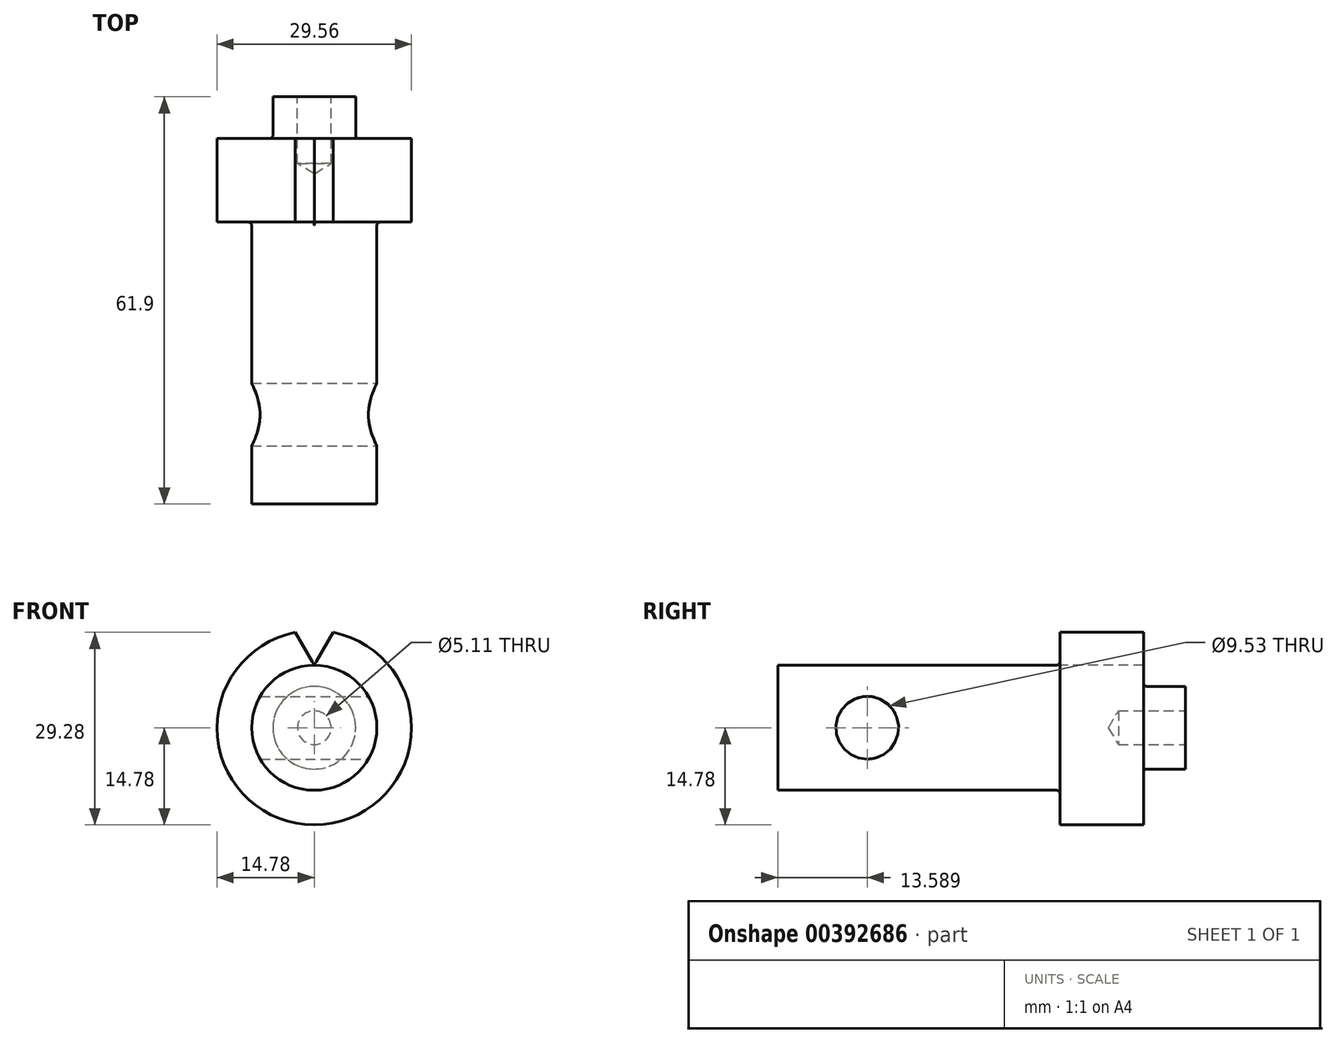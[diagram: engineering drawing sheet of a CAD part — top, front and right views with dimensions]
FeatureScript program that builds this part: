
annotation { "Feature Type Name" : "Feature", "Feature Type Description" : "" }
export const myFeature = defineFeature(function(context is Context, id is Id, definition is map)
    precondition{}
    {
        {
            var Q0;
            Q0=qCreatedBy(makeId("Right.planeOp"),FACE);
            var sketch = newSketch(context, id + "F0", { "sketchPlane" : qUnion([Q0])});
            skLineSegment(sketch, "E0", {"start": v(-42.85, 0) * mm, "end": v(-42.85, 9.51) * mm});
            skLineSegment(sketch, "E1", {"start": v(-42.85, 9.51) * mm, "end": v(0, 9.51) * mm});
            skLineSegment(sketch, "E2", {"start": v(0, 9.51) * mm, "end": v(0, 14.78) * mm});
            skLineSegment(sketch, "E3", {"start": v(0, 14.78) * mm, "end": v(12.7, 14.78) * mm});
            skLineSegment(sketch, "E4", {"start": v(12.7, 14.78) * mm, "end": v(12.7, 6.29) * mm});
            skLineSegment(sketch, "E5", {"start": v(12.7, 6.29) * mm, "end": v(19.05, 6.29) * mm});
            skLineSegment(sketch, "E6", {"start": v(19.05, 6.29) * mm, "end": v(19.05, 0) * mm});
            skLineSegment(sketch, "E7", {"start": v(19.05, 0) * mm, "end": v(-42.85, 0) * mm});
            skSolve(sketch);
        }
        {
            var Q0;
            Q0=makeQuery(id+"F0.imprint","IMPRINT",FACE,{"disambiguationData":[TD([[makeQuery(id+"F0.imprint","IMPRINT",EDGE,{"derivedFrom":sQuery(id+"F0.wireOp",EDGE,"E0")}),-1.0]])]});
            var Q1;
            Q1=sQuery(id+"F0.wireOp",EDGE,"E7");
            revolve(context, id + "F1", {"entities" : qUnion([Q0]), "axis" : qUnion([Q1]), "revolveType" : RevolveType.FULL});
        }
        {
            var Q0;
            Q0=qCreatedBy(makeId("Front.planeOp"),FACE);
            var sketch = newSketch(context, id + "F2", { "sketchPlane" : qUnion([Q0])});
            skLineSegment(sketch, "E8", {"start": v(-2.88, 14.5) * mm, "end": v(0, 9.51) * mm});
            skLineSegment(sketch, "E9", {"start": v(0, 9.51) * mm, "end": v(2.88, 14.5) * mm});
            skArc(sketch, "E10", {"start": v(2.88, 14.5) * mm, "mid": v(0, 14.78) * mm, "end": v(-2.88, 14.5) * mm});
            skSolve(sketch);
        }
        {
            var Q0;
            Q0=makeQuery(id+"F2.imprint","IMPRINT",FACE,{"disambiguationData":[TD([[makeQuery(id+"F2.imprint","IMPRINT",EDGE,{"derivedFrom":sQuery(id+"F2.wireOp",EDGE,"E8")}),1.0]])]});
            extrude(context, id + "F3", {"entities" : qUnion([Q0]), "operationType" : NewBodyOperationType.REMOVE, "oppositeDirection" : true, "depth" : 25.4 * mm});
        }
        {
            var Q0;
            {var subQ2=sQuery(id+"F2.wireOp",EDGE,"E8");var subQ3=makeQuery(id+"F3.boolean.opBoolean","COPY",FACE,{"derivedFrom":makeQuery(id+"F3.opExtrude","SWEPT_FACE",FACE,{"disambiguationData":[OSD([subQ2])]})});var subQ4=sQuery(id+"F0.wireOp",EDGE,"E2");var subQ6=sQuery(id+"F0.wireOp",EDGE,"E1");Q0=makeQuery(id+"Fc7hDyY51l4ybGJ_1.11.F3.boolean.opBoolean","SPLIT",EDGE,{"disambiguationData":[TD([subQ3])],"derivedFrom":makeQuery(id+"Fc7hDyY51l4ybGJ_1.10.F3.boolean.opBoolean","SPLIT",EDGE,{"disambiguationData":[TD([subQ3])],"derivedFrom":makeQuery(id+"Fc7hDyY51l4ybGJ_1.9.F3.boolean.opBoolean","SPLIT",EDGE,{"disambiguationData":[TD([subQ3])],"derivedFrom":makeQuery(id+"Fc7hDyY51l4ybGJ_1.8.F3.boolean.opBoolean","SPLIT",EDGE,{"disambiguationData":[TD([subQ3])],"derivedFrom":makeQuery(id+"Fc7hDyY51l4ybGJ_1.7.F3.boolean.opBoolean","SPLIT",EDGE,{"disambiguationData":[TD([subQ3])],"derivedFrom":makeQuery(id+"Fc7hDyY51l4ybGJ_1.6.F3.boolean.opBoolean","SPLIT",EDGE,{"disambiguationData":[TD([subQ3])],"derivedFrom":makeQuery(id+"Fc7hDyY51l4ybGJ_1.5.F3.boolean.opBoolean","SPLIT",EDGE,{"disambiguationData":[TD([subQ3])],"derivedFrom":makeQuery(id+"Fc7hDyY51l4ybGJ_1.4.F3.boolean.opBoolean","SPLIT",EDGE,{"disambiguationData":[TD([subQ3])],"derivedFrom":makeQuery(id+"Fc7hDyY51l4ybGJ_1.3.F3.boolean.opBoolean","SPLIT",EDGE,{"disambiguationData":[TD([subQ3])],"derivedFrom":makeQuery(id+"Fc7hDyY51l4ybGJ_1.2.F3.boolean.opBoolean","SPLIT",EDGE,{"disambiguationData":[TD([subQ3])],"derivedFrom":makeQuery(id+"Fc7hDyY51l4ybGJ_1.1.F3.boolean.opBoolean","SPLIT",EDGE,{"disambiguationData":[OD(0.0)],"derivedFrom":makeQuery(id+"F1.opRevolve","SWEPT_EDGE",EDGE,{"disambiguationData":[OSD([subQ6,subQ4])]})})})})})})})})})})})});}
            var Q1;
            {var subQ2=sQuery(id+"F2.wireOp",EDGE,"E8");var subQ3=makeQuery(id+"Fc7hDyY51l4ybGJ_1.10.F3.opExtrude","SWEPT_FACE",FACE,{"disambiguationData":[OSD([subQ2])]});var subQ4=sQuery(id+"F0.wireOp",EDGE,"E2");var subQ6=sQuery(id+"F0.wireOp",EDGE,"E1");var subQ9=makeQuery(id+"F3.boolean.opBoolean","COPY",FACE,{"derivedFrom":makeQuery(id+"F3.opExtrude","SWEPT_FACE",FACE,{"disambiguationData":[OSD([subQ2])]})});Q1=makeQuery(id+"Fc7hDyY51l4ybGJ_1.11.F3.boolean.opBoolean","SPLIT",EDGE,{"disambiguationData":[TD([makeQuery(id+"Fc7hDyY51l4ybGJ_1.10.F3.boolean.opBoolean","COPY",FACE,{"derivedFrom":subQ3})])],"derivedFrom":makeQuery(id+"Fc7hDyY51l4ybGJ_1.10.F3.boolean.opBoolean","SPLIT",EDGE,{"disambiguationData":[TD([subQ9])],"derivedFrom":makeQuery(id+"Fc7hDyY51l4ybGJ_1.9.F3.boolean.opBoolean","SPLIT",EDGE,{"disambiguationData":[TD([subQ9])],"derivedFrom":makeQuery(id+"Fc7hDyY51l4ybGJ_1.8.F3.boolean.opBoolean","SPLIT",EDGE,{"disambiguationData":[TD([subQ9])],"derivedFrom":makeQuery(id+"Fc7hDyY51l4ybGJ_1.7.F3.boolean.opBoolean","SPLIT",EDGE,{"disambiguationData":[TD([subQ9])],"derivedFrom":makeQuery(id+"Fc7hDyY51l4ybGJ_1.6.F3.boolean.opBoolean","SPLIT",EDGE,{"disambiguationData":[TD([subQ9])],"derivedFrom":makeQuery(id+"Fc7hDyY51l4ybGJ_1.5.F3.boolean.opBoolean","SPLIT",EDGE,{"disambiguationData":[TD([subQ9])],"derivedFrom":makeQuery(id+"Fc7hDyY51l4ybGJ_1.4.F3.boolean.opBoolean","SPLIT",EDGE,{"disambiguationData":[TD([subQ9])],"derivedFrom":makeQuery(id+"Fc7hDyY51l4ybGJ_1.3.F3.boolean.opBoolean","SPLIT",EDGE,{"disambiguationData":[TD([subQ9])],"derivedFrom":makeQuery(id+"Fc7hDyY51l4ybGJ_1.2.F3.boolean.opBoolean","SPLIT",EDGE,{"disambiguationData":[TD([subQ9])],"derivedFrom":makeQuery(id+"Fc7hDyY51l4ybGJ_1.1.F3.boolean.opBoolean","SPLIT",EDGE,{"disambiguationData":[OD(0.0)],"derivedFrom":makeQuery(id+"F1.opRevolve","SWEPT_EDGE",EDGE,{"disambiguationData":[OSD([subQ6,subQ4])]})})})})})})})})})})})});}
            var Q2;
            {var subQ2=sQuery(id+"F0.wireOp",EDGE,"E1");var subQ4=sQuery(id+"F2.wireOp",EDGE,"E8");var subQ5=makeQuery(id+"Fc7hDyY51l4ybGJ_1.9.F3.opExtrude","SWEPT_FACE",FACE,{"disambiguationData":[OSD([subQ4])]});var subQ6=sQuery(id+"F0.wireOp",EDGE,"E2");var subQ9=makeQuery(id+"F3.boolean.opBoolean","COPY",FACE,{"derivedFrom":makeQuery(id+"F3.opExtrude","SWEPT_FACE",FACE,{"disambiguationData":[OSD([subQ4])]})});Q2=makeQuery(id+"Fc7hDyY51l4ybGJ_1.10.F3.boolean.opBoolean","SPLIT",EDGE,{"disambiguationData":[TD([makeQuery(id+"Fc7hDyY51l4ybGJ_1.9.F3.boolean.opBoolean","COPY",FACE,{"derivedFrom":subQ5})])],"derivedFrom":makeQuery(id+"Fc7hDyY51l4ybGJ_1.9.F3.boolean.opBoolean","SPLIT",EDGE,{"disambiguationData":[TD([subQ9])],"derivedFrom":makeQuery(id+"Fc7hDyY51l4ybGJ_1.8.F3.boolean.opBoolean","SPLIT",EDGE,{"disambiguationData":[TD([subQ9])],"derivedFrom":makeQuery(id+"Fc7hDyY51l4ybGJ_1.7.F3.boolean.opBoolean","SPLIT",EDGE,{"disambiguationData":[TD([subQ9])],"derivedFrom":makeQuery(id+"Fc7hDyY51l4ybGJ_1.6.F3.boolean.opBoolean","SPLIT",EDGE,{"disambiguationData":[TD([subQ9])],"derivedFrom":makeQuery(id+"Fc7hDyY51l4ybGJ_1.5.F3.boolean.opBoolean","SPLIT",EDGE,{"disambiguationData":[TD([subQ9])],"derivedFrom":makeQuery(id+"Fc7hDyY51l4ybGJ_1.4.F3.boolean.opBoolean","SPLIT",EDGE,{"disambiguationData":[TD([subQ9])],"derivedFrom":makeQuery(id+"Fc7hDyY51l4ybGJ_1.3.F3.boolean.opBoolean","SPLIT",EDGE,{"disambiguationData":[TD([subQ9])],"derivedFrom":makeQuery(id+"Fc7hDyY51l4ybGJ_1.2.F3.boolean.opBoolean","SPLIT",EDGE,{"disambiguationData":[TD([subQ9])],"derivedFrom":makeQuery(id+"Fc7hDyY51l4ybGJ_1.1.F3.boolean.opBoolean","SPLIT",EDGE,{"disambiguationData":[OD(0.0)],"derivedFrom":makeQuery(id+"F1.opRevolve","SWEPT_EDGE",EDGE,{"disambiguationData":[OSD([subQ2,subQ6])]})})})})})})})})})})});}
            var Q3;
            {var subQ0=sQuery(id+"F2.wireOp",EDGE,"E8");var subQ1=makeQuery(id+"Fc7hDyY51l4ybGJ_1.8.F3.opExtrude","SWEPT_FACE",FACE,{"disambiguationData":[OSD([subQ0])]});var subQ2=sQuery(id+"F0.wireOp",EDGE,"E2");var subQ6=sQuery(id+"F0.wireOp",EDGE,"E1");var subQ9=makeQuery(id+"F3.boolean.opBoolean","COPY",FACE,{"derivedFrom":makeQuery(id+"F3.opExtrude","SWEPT_FACE",FACE,{"disambiguationData":[OSD([subQ0])]})});Q3=makeQuery(id+"Fc7hDyY51l4ybGJ_1.9.F3.boolean.opBoolean","SPLIT",EDGE,{"disambiguationData":[TD([makeQuery(id+"Fc7hDyY51l4ybGJ_1.8.F3.boolean.opBoolean","COPY",FACE,{"derivedFrom":subQ1})])],"derivedFrom":makeQuery(id+"Fc7hDyY51l4ybGJ_1.8.F3.boolean.opBoolean","SPLIT",EDGE,{"disambiguationData":[TD([subQ9])],"derivedFrom":makeQuery(id+"Fc7hDyY51l4ybGJ_1.7.F3.boolean.opBoolean","SPLIT",EDGE,{"disambiguationData":[TD([subQ9])],"derivedFrom":makeQuery(id+"Fc7hDyY51l4ybGJ_1.6.F3.boolean.opBoolean","SPLIT",EDGE,{"disambiguationData":[TD([subQ9])],"derivedFrom":makeQuery(id+"Fc7hDyY51l4ybGJ_1.5.F3.boolean.opBoolean","SPLIT",EDGE,{"disambiguationData":[TD([subQ9])],"derivedFrom":makeQuery(id+"Fc7hDyY51l4ybGJ_1.4.F3.boolean.opBoolean","SPLIT",EDGE,{"disambiguationData":[TD([subQ9])],"derivedFrom":makeQuery(id+"Fc7hDyY51l4ybGJ_1.3.F3.boolean.opBoolean","SPLIT",EDGE,{"disambiguationData":[TD([subQ9])],"derivedFrom":makeQuery(id+"Fc7hDyY51l4ybGJ_1.2.F3.boolean.opBoolean","SPLIT",EDGE,{"disambiguationData":[TD([subQ9])],"derivedFrom":makeQuery(id+"Fc7hDyY51l4ybGJ_1.1.F3.boolean.opBoolean","SPLIT",EDGE,{"disambiguationData":[OD(0.0)],"derivedFrom":makeQuery(id+"F1.opRevolve","SWEPT_EDGE",EDGE,{"disambiguationData":[OSD([subQ6,subQ2])]})})})})})})})})})});}
            var Q4;
            Q4=makeQuery(id+"Fc7hDyY51l4ybGJ_1.1.F3.boolean.opBoolean","SPLIT",EDGE,{"disambiguationData":[OD(1.0)],"derivedFrom":makeQuery(id+"F1.opRevolve","SWEPT_EDGE",EDGE,{"disambiguationData":[OSD([sQuery(id+"F0.wireOp",EDGE,"E1"),sQuery(id+"F0.wireOp",EDGE,"E2")])]})});
            var Q5;
            {var subQ1=sQuery(id+"F0.wireOp",EDGE,"E2");var subQ2=sQuery(id+"F2.wireOp",EDGE,"E8");var subQ3=sQuery(id+"F0.wireOp",EDGE,"E1");Q5=makeQuery(id+"Fc7hDyY51l4ybGJ_1.2.F3.boolean.opBoolean","SPLIT",EDGE,{"disambiguationData":[TD([makeQuery(id+"Fc7hDyY51l4ybGJ_1.1.F3.boolean.opBoolean","COPY",FACE,{"derivedFrom":makeQuery(id+"Fc7hDyY51l4ybGJ_1.1.F3.opExtrude","SWEPT_FACE",FACE,{"disambiguationData":[OSD([subQ2])]})})])],"derivedFrom":makeQuery(id+"Fc7hDyY51l4ybGJ_1.1.F3.boolean.opBoolean","SPLIT",EDGE,{"disambiguationData":[OD(0.0)],"derivedFrom":makeQuery(id+"F1.opRevolve","SWEPT_EDGE",EDGE,{"disambiguationData":[OSD([subQ3,subQ1])]})})});}
            var Q6;
            {var subQ2=sQuery(id+"F2.wireOp",EDGE,"E8");var subQ3=makeQuery(id+"Fc7hDyY51l4ybGJ_1.2.F3.opExtrude","SWEPT_FACE",FACE,{"disambiguationData":[OSD([subQ2])]});var subQ4=sQuery(id+"F0.wireOp",EDGE,"E2");var subQ6=sQuery(id+"F0.wireOp",EDGE,"E1");Q6=makeQuery(id+"Fc7hDyY51l4ybGJ_1.3.F3.boolean.opBoolean","SPLIT",EDGE,{"disambiguationData":[TD([makeQuery(id+"Fc7hDyY51l4ybGJ_1.2.F3.boolean.opBoolean","COPY",FACE,{"derivedFrom":subQ3})])],"derivedFrom":makeQuery(id+"Fc7hDyY51l4ybGJ_1.2.F3.boolean.opBoolean","SPLIT",EDGE,{"disambiguationData":[TD([makeQuery(id+"F3.boolean.opBoolean","COPY",FACE,{"derivedFrom":makeQuery(id+"F3.opExtrude","SWEPT_FACE",FACE,{"disambiguationData":[OSD([subQ2])]})})])],"derivedFrom":makeQuery(id+"Fc7hDyY51l4ybGJ_1.1.F3.boolean.opBoolean","SPLIT",EDGE,{"disambiguationData":[OD(0.0)],"derivedFrom":makeQuery(id+"F1.opRevolve","SWEPT_EDGE",EDGE,{"disambiguationData":[OSD([subQ6,subQ4])]})})})});}
            var Q7;
            {var subQ0=sQuery(id+"F2.wireOp",EDGE,"E8");var subQ1=makeQuery(id+"Fc7hDyY51l4ybGJ_1.3.F3.opExtrude","SWEPT_FACE",FACE,{"disambiguationData":[OSD([subQ0])]});var subQ2=sQuery(id+"F0.wireOp",EDGE,"E2");var subQ6=sQuery(id+"F0.wireOp",EDGE,"E1");var subQ9=makeQuery(id+"F3.boolean.opBoolean","COPY",FACE,{"derivedFrom":makeQuery(id+"F3.opExtrude","SWEPT_FACE",FACE,{"disambiguationData":[OSD([subQ0])]})});Q7=makeQuery(id+"Fc7hDyY51l4ybGJ_1.4.F3.boolean.opBoolean","SPLIT",EDGE,{"disambiguationData":[TD([makeQuery(id+"Fc7hDyY51l4ybGJ_1.3.F3.boolean.opBoolean","COPY",FACE,{"derivedFrom":subQ1})])],"derivedFrom":makeQuery(id+"Fc7hDyY51l4ybGJ_1.3.F3.boolean.opBoolean","SPLIT",EDGE,{"disambiguationData":[TD([subQ9])],"derivedFrom":makeQuery(id+"Fc7hDyY51l4ybGJ_1.2.F3.boolean.opBoolean","SPLIT",EDGE,{"disambiguationData":[TD([subQ9])],"derivedFrom":makeQuery(id+"Fc7hDyY51l4ybGJ_1.1.F3.boolean.opBoolean","SPLIT",EDGE,{"disambiguationData":[OD(0.0)],"derivedFrom":makeQuery(id+"F1.opRevolve","SWEPT_EDGE",EDGE,{"disambiguationData":[OSD([subQ6,subQ2])]})})})})});}
            var Q8;
            {var subQ2=sQuery(id+"F2.wireOp",EDGE,"E8");var subQ3=makeQuery(id+"Fc7hDyY51l4ybGJ_1.4.F3.opExtrude","SWEPT_FACE",FACE,{"disambiguationData":[OSD([subQ2])]});var subQ4=sQuery(id+"F0.wireOp",EDGE,"E2");var subQ6=sQuery(id+"F0.wireOp",EDGE,"E1");var subQ9=makeQuery(id+"F3.boolean.opBoolean","COPY",FACE,{"derivedFrom":makeQuery(id+"F3.opExtrude","SWEPT_FACE",FACE,{"disambiguationData":[OSD([subQ2])]})});Q8=makeQuery(id+"Fc7hDyY51l4ybGJ_1.5.F3.boolean.opBoolean","SPLIT",EDGE,{"disambiguationData":[TD([makeQuery(id+"Fc7hDyY51l4ybGJ_1.4.F3.boolean.opBoolean","COPY",FACE,{"derivedFrom":subQ3})])],"derivedFrom":makeQuery(id+"Fc7hDyY51l4ybGJ_1.4.F3.boolean.opBoolean","SPLIT",EDGE,{"disambiguationData":[TD([subQ9])],"derivedFrom":makeQuery(id+"Fc7hDyY51l4ybGJ_1.3.F3.boolean.opBoolean","SPLIT",EDGE,{"disambiguationData":[TD([subQ9])],"derivedFrom":makeQuery(id+"Fc7hDyY51l4ybGJ_1.2.F3.boolean.opBoolean","SPLIT",EDGE,{"disambiguationData":[TD([subQ9])],"derivedFrom":makeQuery(id+"Fc7hDyY51l4ybGJ_1.1.F3.boolean.opBoolean","SPLIT",EDGE,{"disambiguationData":[OD(0.0)],"derivedFrom":makeQuery(id+"F1.opRevolve","SWEPT_EDGE",EDGE,{"disambiguationData":[OSD([subQ6,subQ4])]})})})})})});}
            var Q9;
            {var subQ2=sQuery(id+"F0.wireOp",EDGE,"E2");var subQ4=sQuery(id+"F2.wireOp",EDGE,"E8");var subQ5=makeQuery(id+"Fc7hDyY51l4ybGJ_1.5.F3.opExtrude","SWEPT_FACE",FACE,{"disambiguationData":[OSD([subQ4])]});var subQ6=sQuery(id+"F0.wireOp",EDGE,"E1");var subQ9=makeQuery(id+"F3.boolean.opBoolean","COPY",FACE,{"derivedFrom":makeQuery(id+"F3.opExtrude","SWEPT_FACE",FACE,{"disambiguationData":[OSD([subQ4])]})});Q9=makeQuery(id+"Fc7hDyY51l4ybGJ_1.6.F3.boolean.opBoolean","SPLIT",EDGE,{"disambiguationData":[TD([makeQuery(id+"Fc7hDyY51l4ybGJ_1.5.F3.boolean.opBoolean","COPY",FACE,{"derivedFrom":subQ5})])],"derivedFrom":makeQuery(id+"Fc7hDyY51l4ybGJ_1.5.F3.boolean.opBoolean","SPLIT",EDGE,{"disambiguationData":[TD([subQ9])],"derivedFrom":makeQuery(id+"Fc7hDyY51l4ybGJ_1.4.F3.boolean.opBoolean","SPLIT",EDGE,{"disambiguationData":[TD([subQ9])],"derivedFrom":makeQuery(id+"Fc7hDyY51l4ybGJ_1.3.F3.boolean.opBoolean","SPLIT",EDGE,{"disambiguationData":[TD([subQ9])],"derivedFrom":makeQuery(id+"Fc7hDyY51l4ybGJ_1.2.F3.boolean.opBoolean","SPLIT",EDGE,{"disambiguationData":[TD([subQ9])],"derivedFrom":makeQuery(id+"Fc7hDyY51l4ybGJ_1.1.F3.boolean.opBoolean","SPLIT",EDGE,{"disambiguationData":[OD(0.0)],"derivedFrom":makeQuery(id+"F1.opRevolve","SWEPT_EDGE",EDGE,{"disambiguationData":[OSD([subQ6,subQ2])]})})})})})})});}
            var Q10;
            {var subQ2=sQuery(id+"F0.wireOp",EDGE,"E2");var subQ4=sQuery(id+"F2.wireOp",EDGE,"E8");var subQ5=makeQuery(id+"Fc7hDyY51l4ybGJ_1.6.F3.opExtrude","SWEPT_FACE",FACE,{"disambiguationData":[OSD([subQ4])]});var subQ6=sQuery(id+"F0.wireOp",EDGE,"E1");var subQ9=makeQuery(id+"F3.boolean.opBoolean","COPY",FACE,{"derivedFrom":makeQuery(id+"F3.opExtrude","SWEPT_FACE",FACE,{"disambiguationData":[OSD([subQ4])]})});Q10=makeQuery(id+"Fc7hDyY51l4ybGJ_1.7.F3.boolean.opBoolean","SPLIT",EDGE,{"disambiguationData":[TD([makeQuery(id+"Fc7hDyY51l4ybGJ_1.6.F3.boolean.opBoolean","COPY",FACE,{"derivedFrom":subQ5})])],"derivedFrom":makeQuery(id+"Fc7hDyY51l4ybGJ_1.6.F3.boolean.opBoolean","SPLIT",EDGE,{"disambiguationData":[TD([subQ9])],"derivedFrom":makeQuery(id+"Fc7hDyY51l4ybGJ_1.5.F3.boolean.opBoolean","SPLIT",EDGE,{"disambiguationData":[TD([subQ9])],"derivedFrom":makeQuery(id+"Fc7hDyY51l4ybGJ_1.4.F3.boolean.opBoolean","SPLIT",EDGE,{"disambiguationData":[TD([subQ9])],"derivedFrom":makeQuery(id+"Fc7hDyY51l4ybGJ_1.3.F3.boolean.opBoolean","SPLIT",EDGE,{"disambiguationData":[TD([subQ9])],"derivedFrom":makeQuery(id+"Fc7hDyY51l4ybGJ_1.2.F3.boolean.opBoolean","SPLIT",EDGE,{"disambiguationData":[TD([subQ9])],"derivedFrom":makeQuery(id+"Fc7hDyY51l4ybGJ_1.1.F3.boolean.opBoolean","SPLIT",EDGE,{"disambiguationData":[OD(0.0)],"derivedFrom":makeQuery(id+"F1.opRevolve","SWEPT_EDGE",EDGE,{"disambiguationData":[OSD([subQ6,subQ2])]})})})})})})})});}
            var Q11;
            {var subQ2=sQuery(id+"F2.wireOp",EDGE,"E8");var subQ3=makeQuery(id+"Fc7hDyY51l4ybGJ_1.7.F3.opExtrude","SWEPT_FACE",FACE,{"disambiguationData":[OSD([subQ2])]});var subQ4=sQuery(id+"F0.wireOp",EDGE,"E2");var subQ6=sQuery(id+"F0.wireOp",EDGE,"E1");var subQ9=makeQuery(id+"F3.boolean.opBoolean","COPY",FACE,{"derivedFrom":makeQuery(id+"F3.opExtrude","SWEPT_FACE",FACE,{"disambiguationData":[OSD([subQ2])]})});Q11=makeQuery(id+"Fc7hDyY51l4ybGJ_1.8.F3.boolean.opBoolean","SPLIT",EDGE,{"disambiguationData":[TD([makeQuery(id+"Fc7hDyY51l4ybGJ_1.7.F3.boolean.opBoolean","COPY",FACE,{"derivedFrom":subQ3})])],"derivedFrom":makeQuery(id+"Fc7hDyY51l4ybGJ_1.7.F3.boolean.opBoolean","SPLIT",EDGE,{"disambiguationData":[TD([subQ9])],"derivedFrom":makeQuery(id+"Fc7hDyY51l4ybGJ_1.6.F3.boolean.opBoolean","SPLIT",EDGE,{"disambiguationData":[TD([subQ9])],"derivedFrom":makeQuery(id+"Fc7hDyY51l4ybGJ_1.5.F3.boolean.opBoolean","SPLIT",EDGE,{"disambiguationData":[TD([subQ9])],"derivedFrom":makeQuery(id+"Fc7hDyY51l4ybGJ_1.4.F3.boolean.opBoolean","SPLIT",EDGE,{"disambiguationData":[TD([subQ9])],"derivedFrom":makeQuery(id+"Fc7hDyY51l4ybGJ_1.3.F3.boolean.opBoolean","SPLIT",EDGE,{"disambiguationData":[TD([subQ9])],"derivedFrom":makeQuery(id+"Fc7hDyY51l4ybGJ_1.2.F3.boolean.opBoolean","SPLIT",EDGE,{"disambiguationData":[TD([subQ9])],"derivedFrom":makeQuery(id+"Fc7hDyY51l4ybGJ_1.1.F3.boolean.opBoolean","SPLIT",EDGE,{"disambiguationData":[OD(0.0)],"derivedFrom":makeQuery(id+"F1.opRevolve","SWEPT_EDGE",EDGE,{"disambiguationData":[OSD([subQ6,subQ4])]})})})})})})})})});}
            var Q12;
            Q12=makeQuery(id+"F1.opRevolve","SWEPT_EDGE",EDGE,{"disambiguationData":[OSD([sQuery(id+"F0.wireOp",EDGE,"E4"),sQuery(id+"F0.wireOp",EDGE,"E5")])]});
            fillet(context, id + "F4", {"entities" : qUnion([Q0, Q1, Q2, Q3, Q4, Q5, Q6, Q7, Q8, Q9, Q10, Q11, Q12]), "radius" : 0.5 * mm, "tangentPropagation" : true, "allowEdgeOverflow" : false});
        }
        {
            var Q0;
            Q0=makeQuery(id+"F1.opRevolve","SWEPT_FACE",FACE,{"disambiguationData":[OSD([sQuery(id+"F0.wireOp",EDGE,"E6")])]});
            var sketch = newSketch(context, id + "F5", { "sketchPlane" : qUnion([Q0])});
            skPoint(sketch, "E11", {"position": v(0, 0) * mm});
            skSolve(sketch);
        }
        {
            var Q0;
            Q0=sQuery(id+"F5.wireOp",VERTEX,"E11");
            var Q1;
            Q1=makeQuery(id+"F1.opRevolve","SWEPT_BODY",BODY,{"disambiguationData":[OSD([sQuery(id+"F0.wireOp",EDGE,"E0"),sQuery(id+"F0.wireOp",EDGE,"E1"),sQuery(id+"F0.wireOp",EDGE,"E2"),sQuery(id+"F0.wireOp",EDGE,"E3"),sQuery(id+"F0.wireOp",EDGE,"E4"),sQuery(id+"F0.wireOp",EDGE,"E5"),sQuery(id+"F0.wireOp",EDGE,"E6"),sQuery(id+"F0.wireOp",EDGE,"E7")])]});
            hole(context, id + "F6", {"style" : HoleStyle.SIMPLE, "endStyle" : HoleEndStyle.BLIND, "standardTappedOrClearance" : lookupTablePath({ "standard" : "ANSI", "engagement" : "75%", "pitch" : "20 tpi", "size" : "1/4", "type" : "Tapped" }), "standardBlindInLast" : lookupTablePath({ "standard" : "ANSI", "engagement" : "75%", "pitch" : "20 tpi", "size" : "1/4", "type" : "Tapped" }), "holeDiameter" : 5.1 * mm, "showTappedDepth" : true, "holeDepth" : 10.16 * mm, "isTappedThrough" : true, "tappedDepth" : 6.35 * mm, "tapClearance" : 3, "locations" : qUnion([Q0]), "scope" : qUnion([Q1]), "majorDiameter" : 6.35 * mm});
        }
        {
            var Q0;
            Q0=qCreatedBy(makeId("Right.planeOp"),FACE);
            cPlane(context, id + "F7", {"entities" : qUnion([Q0]), "cplaneType" : CPlaneType.OFFSET, "offset" : 9.5 * mm, "width" : 152.4 * mm, "height" : 152.4 * mm});
        }
        {
            var Q0;
            Q0=qCreatedBy(id+"F7.planeOp",FACE);
            var sketch = newSketch(context, id + "F8", { "sketchPlane" : qUnion([Q0])});
            skPoint(sketch, "E12", {"position": v(-29.26, 0) * mm});
            skSolve(sketch);
        }
        {
            var Q0;
            Q0=sQuery(id+"F8.wireOp",VERTEX,"E12");
            var Q1;
            Q1=makeQuery(id+"F1.opRevolve","SWEPT_BODY",BODY,{"disambiguationData":[OSD([sQuery(id+"F0.wireOp",EDGE,"E0"),sQuery(id+"F0.wireOp",EDGE,"E1"),sQuery(id+"F0.wireOp",EDGE,"E2"),sQuery(id+"F0.wireOp",EDGE,"E3"),sQuery(id+"F0.wireOp",EDGE,"E4"),sQuery(id+"F0.wireOp",EDGE,"E5"),sQuery(id+"F0.wireOp",EDGE,"E6"),sQuery(id+"F0.wireOp",EDGE,"E7")])]});
            hole(context, id + "F9", {"style" : HoleStyle.SIMPLE, "endStyle" : HoleEndStyle.THROUGH, "holeDiameter" : 9.52 * mm, "isTappedThrough" : true, "tappedDepth" : 6.35 * mm, "tapClearance" : 3, "locations" : qUnion([Q0]), "scope" : qUnion([Q1])});
        }
    });
